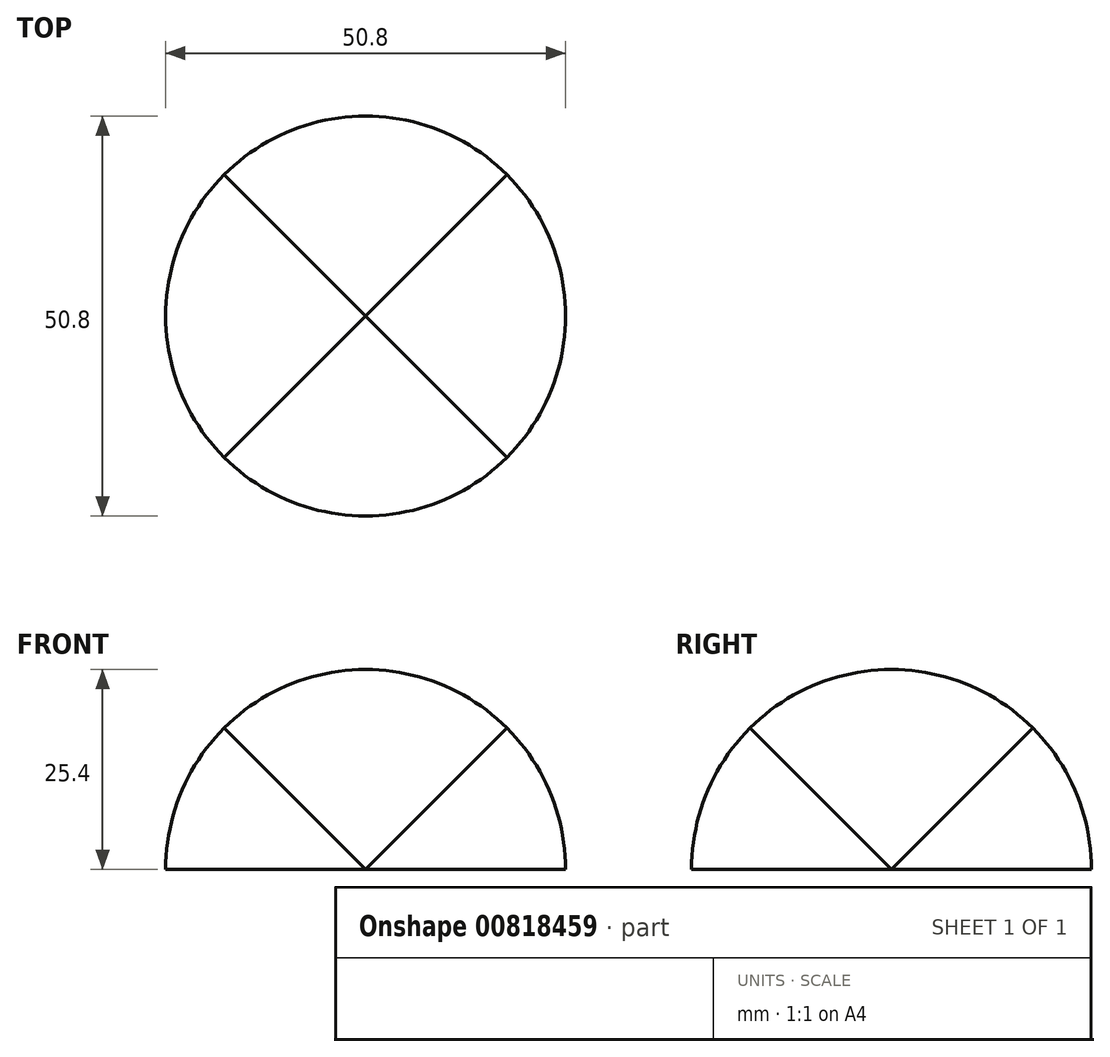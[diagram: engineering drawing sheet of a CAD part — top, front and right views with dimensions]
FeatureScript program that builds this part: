
annotation { "Feature Type Name" : "Feature", "Feature Type Description" : "" }
export const myFeature = defineFeature(function(context is Context, id is Id, definition is map)
    precondition{}
    {
        {
            var Q0;
            Q0=qCreatedBy(makeId("Top.planeOp"),FACE);
            var sketch = newSketch(context, id + "F0", { "sketchPlane" : qUnion([Q0])});
            skLineSegment(sketch, "E0", {"start": v(-25.4, 0) * mm, "end": v(-25.4, 25.4) * mm});
            skLineSegment(sketch, "E1", {"start": v(-25.4, 25.4) * mm, "end": v(0, 25.4) * mm});
            skLineSegment(sketch, "E2.MirrorCS", {"start": v(25.4, 0) * mm, "end": v(25.4, 25.4) * mm});
            skLineSegment(sketch, "E3.MirrorCS", {"start": v(25.4, 25.4) * mm, "end": v(0, 25.4) * mm});
            skLineSegment(sketch, "E4.MirrorCS", {"start": v(-25.4, 0) * mm, "end": v(-25.4, -25.4) * mm});
            skLineSegment(sketch, "E5.MirrorCS", {"start": v(-25.4, -25.4) * mm, "end": v(0, -25.4) * mm});
            skLineSegment(sketch, "E6.MirrorCS", {"start": v(25.4, -25.4) * mm, "end": v(0, -25.4) * mm});
            skLineSegment(sketch, "E7.MirrorCS", {"start": v(25.4, 0) * mm, "end": v(25.4, -25.4) * mm});
            skSolve(sketch);
        }
        {
            var Q0;
            Q0 = qSketchRegion(id + "F0", true);
            extrude(context, id + "F1", {"entities" : qUnion([Q0]), "depth" : 25.4 * mm, "offsetDistance" : 25.4 * mm});
        }
        {
            var Q0;
            Q0=qCreatedBy(makeId("Top.planeOp"),FACE);
            var sketch = newSketch(context, id + "F2", { "sketchPlane" : qUnion([Q0])});
            skCircle(sketch, "E8", {"center": v(0, 0) * mm, "radius": 25.4 * mm});
            skCircle(sketch, "E9", {"center": v(0, 0) * mm, "radius": 38.1 * mm});
            skSolve(sketch);
        }
        {
            var Q0;
            Q0 = qSketchRegion(id + "F2", true);
            extrude(context, id + "F3", {"entities" : qUnion([Q0]), "operationType" : NewBodyOperationType.REMOVE, "endBound" : BoundingType.SYMMETRIC, "oppositeDirection" : true, "depth" : 50.8 * mm, "offsetDistance" : 25.4 * mm});
        }
        {
            var Q0;
            Q0=qCreatedBy(makeId("Front.planeOp"),FACE);
            var sketch = newSketch(context, id + "F4", { "sketchPlane" : qUnion([Q0])});
            skCircle(sketch, "E10", {"center": v(0, 0) * mm, "radius": 25.4 * mm});
            skSolve(sketch);
        }
        {
            var Q0;
            Q0 = qSketchRegion(id + "F4", true);
            extrude(context, id + "F5", {"entities" : qUnion([Q0]), "operationType" : NewBodyOperationType.INTERSECT, "endBound" : BoundingType.SYMMETRIC, "oppositeDirection" : true, "depth" : 50.8 * mm, "offsetDistance" : 25.4 * mm});
        }
        {
            var Q0;
            Q0=qCreatedBy(makeId("Right.planeOp"),FACE);
            var sketch = newSketch(context, id + "F6", { "sketchPlane" : qUnion([Q0])});
            skCircle(sketch, "E11", {"center": v(0, 0) * mm, "radius": 25.4 * mm});
            skSolve(sketch);
        }
        {
            var Q0;
            Q0 = qSketchRegion(id + "F6", true);
            extrude(context, id + "F7", {"entities" : qUnion([Q0]), "operationType" : NewBodyOperationType.INTERSECT, "endBound" : BoundingType.SYMMETRIC, "depth" : 50.8 * mm, "offsetDistance" : 25.4 * mm});
        }
    });
